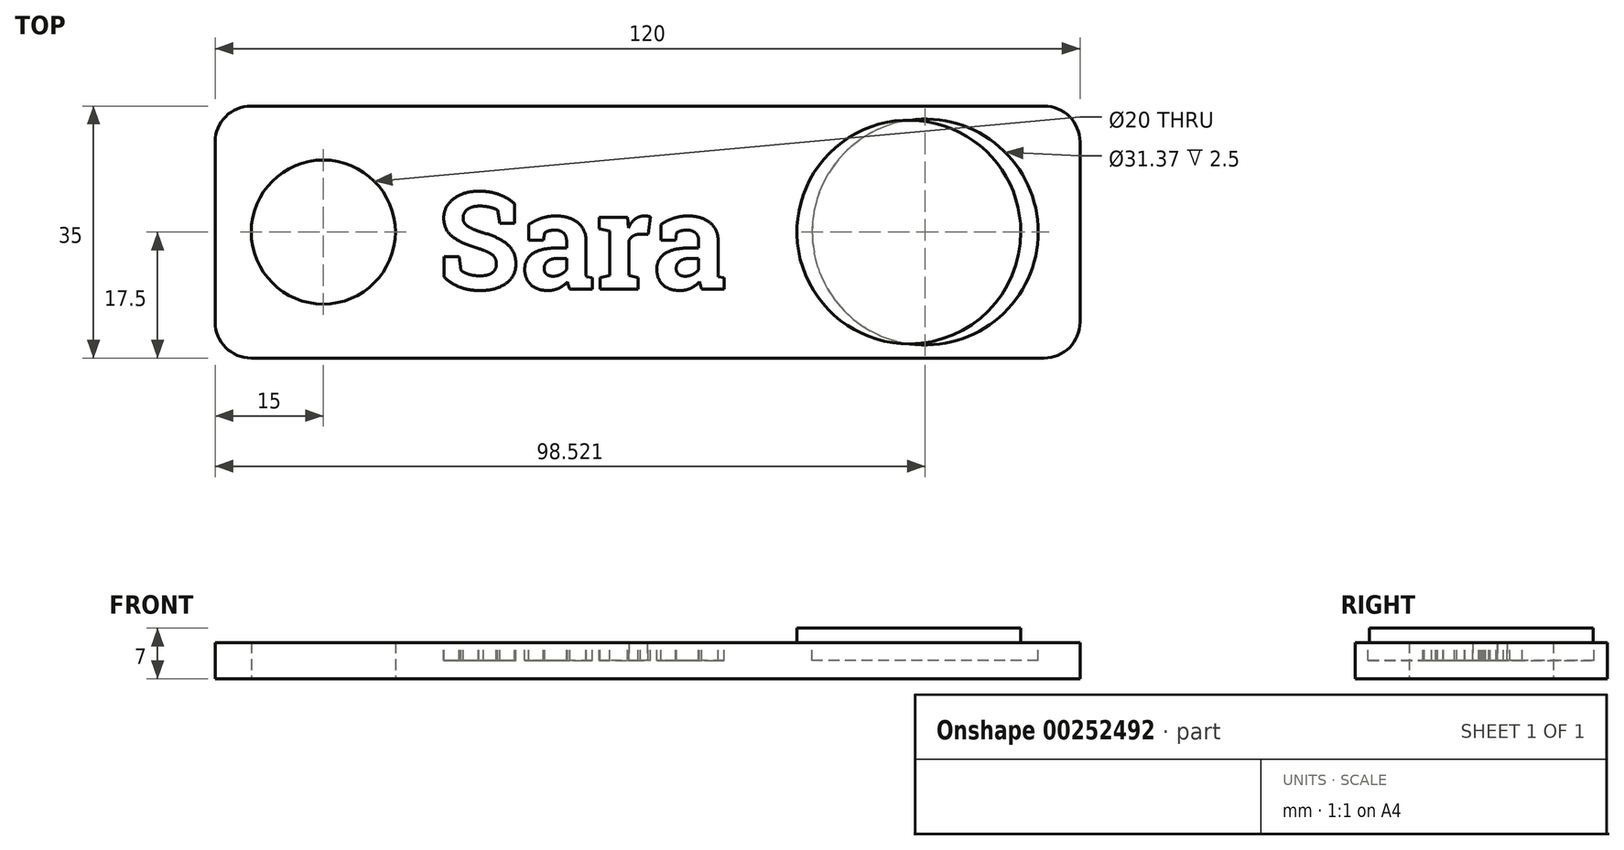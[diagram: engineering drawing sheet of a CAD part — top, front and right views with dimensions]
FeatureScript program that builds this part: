
annotation { "Feature Type Name" : "Feature", "Feature Type Description" : "" }
export const myFeature = defineFeature(function(context is Context, id is Id, definition is map)
    precondition{}
    {
        {
            var Q0;
            Q0=qCreatedBy(makeId("Top.planeOp"),FACE);
            var sketch = newSketch(context, id + "F0", { "sketchPlane" : qUnion([Q0])});
            skLineSegment(sketch, "E0.bottom", {"start": v(60, -17.5) * mm, "end": v(-60, -17.5) * mm});
            skLineSegment(sketch, "E0.top", {"start": v(60, 17.5) * mm, "end": v(-60, 17.5) * mm});
            skLineSegment(sketch, "E0.left", {"start": v(60, -17.5) * mm, "end": v(60, 17.5) * mm});
            skLineSegment(sketch, "E0.right", {"start": v(-60, -17.5) * mm, "end": v(-60, 17.5) * mm});
            skPoint(sketch, "E0.middle", {"position": v(0, 0) * mm});
            skCircle(sketch, "E1", {"center": v(-45, 0) * mm, "radius": 10 * mm});
            skSolve(sketch);
        }
        {
            var Q0;
            Q0=makeQuery(id+"F0.imprint","IMPRINT",FACE,{"disambiguationData":[TD([[makeQuery(id+"F0.imprint","IMPRINT",EDGE,{"derivedFrom":sQuery(id+"F0.wireOp",EDGE,"E0.bottom")}),-1.0]])]});
            extrude(context, id + "F1", {"entities" : qUnion([Q0]), "depth" : 5 * mm});
        }
        {
            var Q0;
            Q0=makeQuery(id+"F1.opExtrude","SWEPT_EDGE",EDGE,{"disambiguationData":[OSD([sQuery(id+"F0.wireOp",EDGE,"E0.bottom"),sQuery(id+"F0.wireOp",EDGE,"E0.left")])]});
            var Q1;
            Q1=makeQuery(id+"F1.opExtrude","SWEPT_EDGE",EDGE,{"disambiguationData":[OSD([sQuery(id+"F0.wireOp",EDGE,"E0.top"),sQuery(id+"F0.wireOp",EDGE,"E0.left")])]});
            var Q2;
            Q2=makeQuery(id+"F1.opExtrude","SWEPT_EDGE",EDGE,{"disambiguationData":[OSD([sQuery(id+"F0.wireOp",EDGE,"E0.bottom"),sQuery(id+"F0.wireOp",EDGE,"E0.right")])]});
            fillet(context, id + "F2", {"entities" : qUnion([Q0, Q1, Q2]), "radius" : 5 * mm, "tangentPropagation" : true, "allowEdgeOverflow" : false});
        }
        {
            var Q0;
            Q0=makeQuery(id+"F1.opExtrude","SWEPT_EDGE",EDGE,{"disambiguationData":[OSD([sQuery(id+"F0.wireOp",EDGE,"E0.top"),sQuery(id+"F0.wireOp",EDGE,"E0.right")])]});
            fillet(context, id + "F3", {"entities" : qUnion([Q0]), "radius" : 5 * mm, "tangentPropagation" : true, "allowEdgeOverflow" : false});
        }
        {
            var Q0;
            Q0=makeQuery(id+"F1.opExtrude","CAP_FACE",FACE,{"disambiguationData":[OSD([sQuery(id+"F0.wireOp",EDGE,"E0.bottom"),sQuery(id+"F0.wireOp",EDGE,"E0.top"),sQuery(id+"F0.wireOp",EDGE,"E0.left"),sQuery(id+"F0.wireOp",EDGE,"E0.right"),sQuery(id+"F0.wireOp",EDGE,"E1")])],"isStart":false});
            var sketch = newSketch(context, id + "F4", { "sketchPlane" : qUnion([Q0])});
            skText(sketch, "E2", { "text": "Sara", "fontName": "RobotoSlab-Bold.ttf"});
            skCircle(sketch, "E3", {"center": v(38.52, 0) * mm, "radius": 15.68 * mm});
            const initialGuessF4  = {"E2": [-0.02918, -0.00793, 1, 0, 0.0136]};
            skSetInitialGuess(sketch, initialGuessF4);
            skSolve(sketch);
        }
        {
            var Q0;
            Q0 = qSketchRegion(id + "F4", true);
            extrude(context, id + "F5", {"entities" : qUnion([Q0]), "operationType" : NewBodyOperationType.REMOVE, "oppositeDirection" : true, "depth" : 2.5 * mm});
        }
        {
            var Q0;
            {var subQ0=sQuery(id+"F0.wireOp",EDGE,"E0.right");var subQ1=sQuery(id+"F0.wireOp",EDGE,"E0.top");var subQ2=sQuery(id+"F0.wireOp",EDGE,"E0.bottom");var subQ3=sQuery(id+"F0.wireOp",EDGE,"E0.left");var subQ4=sQuery(id+"F0.wireOp",EDGE,"E1");Q0=makeQuery(id+"F5.boolean.opBoolean","SPLIT",FACE,{"disambiguationData":[TD([makeQuery(id+"F1.opExtrude","SWEPT_FACE",FACE,{"disambiguationData":[OSD([subQ2])]})])],"derivedFrom":makeQuery(id+"F1.opExtrude","CAP_FACE",FACE,{"disambiguationData":[OSD([subQ2,subQ1,subQ3,subQ0,subQ4])],"isStart":false})});}
            var sketch = newSketch(context, id + "F6", { "sketchPlane" : qUnion([Q0])});
            skSolve(sketch);
        }
        {
            var Q0;
            {var subQ1=sQuery(id+"F0.wireOp",EDGE,"E1");Q0=makeQuery(id+"F6.imprint","IMPRINT",FACE,{"disambiguationData":[TD([[makeQuery(id+"F6.imprint","IMPRINT",EDGE,{"derivedFrom":makeQuery(id+"F1.opExtrude","CAP_EDGE",EDGE,{"disambiguationData":[OSD([subQ1])],"isStart":false})}),-1.0]])]});}
            var sketch = newSketch(context, id + "F7", { "sketchPlane" : qUnion([Q0])});
            skCircle(sketch, "E4", {"center": v(36.26, 0) * mm, "radius": 15.53 * mm});
            skSolve(sketch);
        }
        {
            var Q0;
            Q0 = qSketchRegion(id + "F7", true);
            extrude(context, id + "F8", {"entities" : qUnion([Q0]), "operationType" : NewBodyOperationType.ADD, "depth" : 2 * mm});
        }
    });
